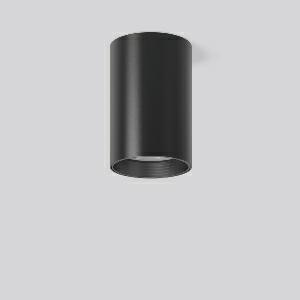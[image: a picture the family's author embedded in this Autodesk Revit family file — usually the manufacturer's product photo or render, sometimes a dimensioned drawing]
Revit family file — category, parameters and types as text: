
# Revit family: heledon_maxi_a_931220_003_76_aa6b
name_source: partatom
category: Lighting Fixtures
units: mm (PartAtom-declared; Revit-internal decimal feet)

## family parameters
Cut with Voids When Loaded = No
Host = Face
Light Source = No
Part Type = Normal
Room Calculation Point = No
Round Connector Dimension = Use Diameter
Shared = No

## types (1)
- HELEDON maxi A (1 x LED Modul 930, 2850 lm, 3000)
    Apparent Load = 25 VA
    Approval mark = CE
    CIE Flux Codes = 97 100 100 100 100
    Color Rendering = 90
    Color Temperature = 3000
    Default Elevation = 1800 mm
    Description = Series: HELEDON maxi
Cylindrical surface-mounted downlight. Housing: die-cast aluminium, powder-coated. Internal ceiling frame polycarbonate with bayonet mounting. Black plastic ring and recessed LED to prevent glare from the side. Optical assembly with lens made of plastic (polycarbonate) for the best homogeneous light distribution - can be changed without tools. Best colour rendering index Ra>90. Suitable for Ceiling mounting. Easy installation with a separate ceiling frame with bayonet mounting and plug connection. Driver integrated. Connected via plug-in connector. High quality converter without flickering and stroboscopic effect. The following accessories can be mounted without use of tools: interchangeable lenses, decorative glasses, honeycomb louvre, clear and frosted diffusers, white interchangeable plastic ring. 
Colour: deep black, matt (RAL 9005)
Diameter: 123 mm
Height: 183 mm
Lamp: LED
Socket: without socket
Colour temperature: 3000K
Colour rendering index (CRI): 92
System power: 25 W
Rated luminous flux: 2850 lm
Luminous efficiency: 114 lm/W
Control gear: Converter, dimmable, DALI
Protection class: I
Type of protection: IP 20
    Height = 183 mm
    Lamp = 1 x LED Modul 930
    Lamp Light Flux = 2850 lm
    Lamp count = 1
    Length = 123 mm
    Lifetime = 50000 h
    Luminous efficacy = 114 lm/W
    Manufacturer = RZB
    ModVariant = No
    Model = 931220.003.76
    Mounting Place = Ceiling
    Mounting Type = Surface mounted
    Number of Poles = 1
    OnlyDefault = Yes
    Power Factor = 1
    Product Name = HELEDON maxi A
    Product group = Surface mounted downlights
    ProductGroupID = 302
    Protection Class = Protection class I
    Protection Degree = IP 20
    RLX_Detail_Level = 1
    RLX_Emergency_Light_Flux = 0 lm
    RLX_Emergency_Type = 0
    RLX_Emergency_Type_DB = No
    RlxData = <blob elided: 98073 chars, md5=be3dd9d1>
    Socket = socket
    Standby Power = 0 W
    System Light Flux = 2850 lm
    System Power = 25 W
    Type Comments = Product without accessories
    Type Image = 931193.003.jpg
    URL = http://relux.com
    VarID = ---
    Voltage = 230 V
    Voltage Range = 220-240 V
    Weight = 0.00 kg
    Width = 0 mm  [stored 0 ft]

note: [stored X ft] marks values corroborated as IEEE doubles in the binary element streams (Revit-internal decimal feet)

## geometry (parser evidence)
native form markers: Blend x4, Sweep x8
no freeform markers — native parametric forms only
